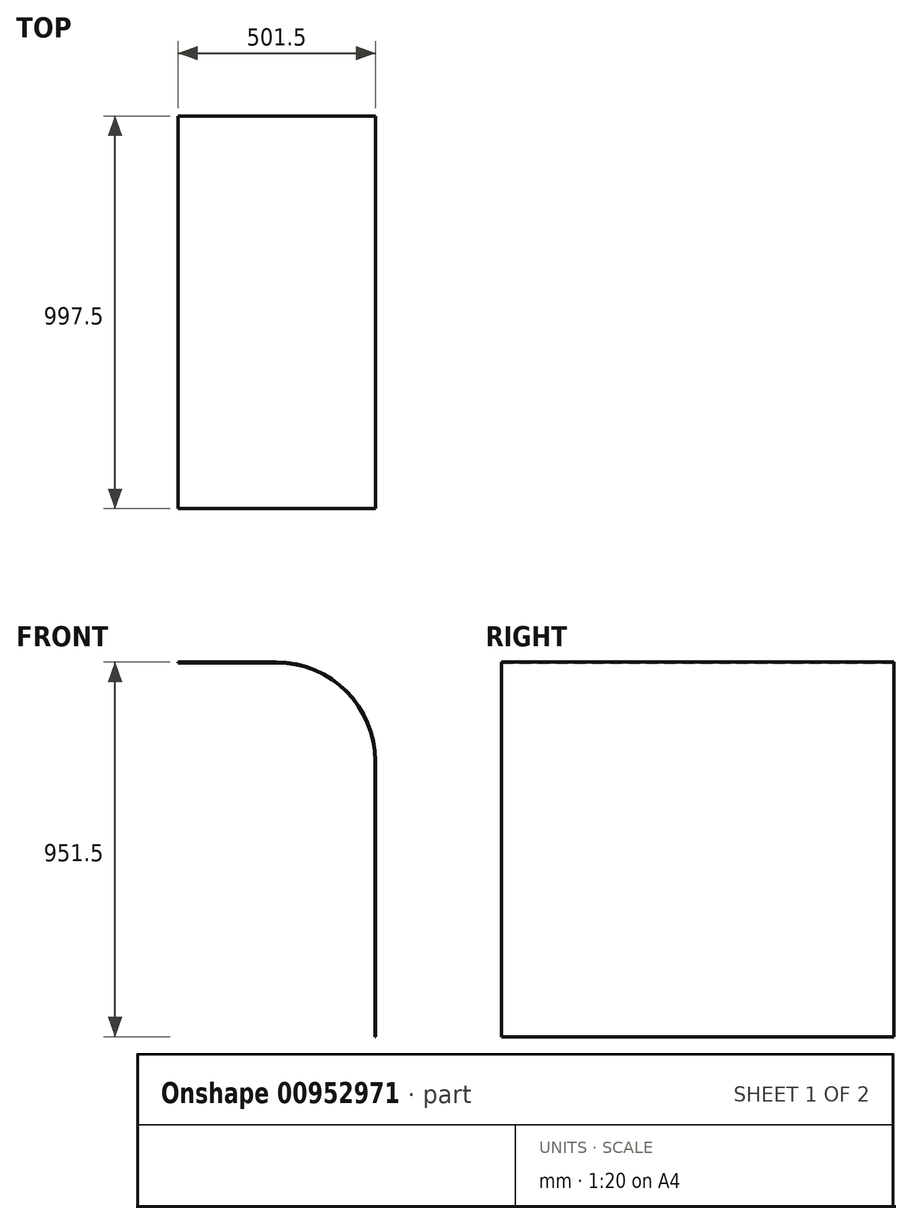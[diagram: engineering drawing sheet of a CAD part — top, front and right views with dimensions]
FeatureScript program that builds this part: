
annotation { "Feature Type Name" : "Feature", "Feature Type Description" : "" }
export const myFeature = defineFeature(function(context is Context, id is Id, definition is map)
    precondition{}
    {
        {
            var Q0;
            Q0=qCreatedBy(makeId("Front.planeOp"),FACE);
            var sketch = newSketch(context, id + "F0", { "sketchPlane" : qUnion([Q0])});
            skLineSegment(sketch, "E0", {"start": v(0, 0) * mm, "end": v(-700, 0) * mm});
            skLineSegment(sketch, "E1", {"start": v(-700, 0) * mm, "end": v(-700, 700) * mm});
            skLineSegment(sketch, "E2", {"start": v(-700, 700) * mm, "end": v(-950, 700) * mm});
            skCircle(sketch, "E3", {"center": v(-700, 700) * mm, "radius": 250 * mm});
            skLineSegment(sketch, "E4", {"start": v(-450, 700) * mm, "end": v(-450, 0) * mm});
            skLineSegment(sketch, "E5", {"start": v(-950, 700) * mm, "end": v(-950, 1650) * mm});
            skLineSegment(sketch, "E6", {"start": v(-950, 950) * mm, "end": v(-700, 950) * mm});
            skLineSegment(sketch, "E7", {"start": v(-450, 0) * mm, "end": v(250, 0) * mm});
            skLineSegment(sketch, "E8", {"start": v(250, 0) * mm, "end": v(250, 1150) * mm});
            skLineSegment(sketch, "E9", {"start": v(-950, 1650) * mm, "end": v(-250, 1650) * mm});
            skPoint(sketch, "E10.visualSharp", {"position": v(250, 1650) * mm});
            skArc(sketch, "E10.filletArc", {"start": v(250, 1150) * mm, "mid": v(103.55, 1503.55) * mm, "end": v(-250, 1650) * mm});
            skLineSegment(sketch, "E11", {"start": v(-950, 950) * mm, "end": v(-1650, 1650) * mm});
            skLineSegment(sketch, "E12", {"start": v(-950, 1650) * mm, "end": v(-1650, 1650) * mm});
            skArc(sketch, "E13", {"start": v(-450, 700) * mm, "mid": v(-523.22, 876.78) * mm, "end": v(-700, 950) * mm});
            skLineSegment(sketch, "E14.0", {"start": v(-950, 1648.75) * mm, "end": v(-1650, 1648.75) * mm});
            skLineSegment(sketch, "E14.1", {"start": v(-950, 1648.75) * mm, "end": v(-250, 1648.75) * mm});
            skArc(sketch, "E14.2", {"start": v(248.75, 1150) * mm, "mid": v(102.67, 1502.67) * mm, "end": v(-250, 1648.75) * mm});
            skLineSegment(sketch, "E14.3", {"start": v(248.75, 0) * mm, "end": v(248.75, 1150) * mm});
            skLineSegment(sketch, "E15.0", {"start": v(-448.5, 700) * mm, "end": v(-448.5, 0) * mm});
            skArc(sketch, "E15.1", {"start": v(-448.5, 700) * mm, "mid": v(-522.16, 877.84) * mm, "end": v(-700, 951.5) * mm});
            skLineSegment(sketch, "E15.2", {"start": v(-950, 951.5) * mm, "end": v(-700, 951.5) * mm});
            skSolve(sketch);
        }
        {
            var Q0;
            {var subQ3=sQuery(id+"F0.wireOp",EDGE,"E4");Q0=makeQuery(id+"F0.imprint","IMPRINT",FACE,{"disambiguationData":[TD([[makeQuery(id+"F0.imprint","IMPRINT",EDGE,{"derivedFrom":subQ3}),1.0]])]});}
            extrude(context, id + "F1", {"entities" : qUnion([Q0]), "depth" : (1000 - 2.5) * mm, "offsetDistance" : 25 * mm});
        }
    });
